# Revit family: DIGIDIM Mini Input Unit _444
name_source: partatom
category: Electrical Fixtures
revit_build: Autodesk Revit 2018 (Build: 20170223_1515(x64)
units: mm (PartAtom-declared; Revit-internal decimal feet)

## family parameters
Always vertical = No
Cut with Voids When Loaded = No
Maintain Annotation Orientation = No
OmniClass Number = 23.80.00.00
OmniClass Title = Electric Power and Lighting
Part Type = Normal
Room Calculation Point = No
Round Connector Dimension = Use Diameter
Shared = No
Work Plane-Based = Yes

## types (1)
- Mini Input UNIT
    Ambient temperature = 0 °C to +40 °C
    Cable length = 170mm. Do NOT increase length of switch input cable.
    DALI Connection = Ribbon cable terminated with
1.2 mm ferrules.
    DALI consumption = 10 mA
    DALI supply output = None (Use external DALI power supply.)
    Debounce period = 50 ms
    Default Elevation = 0 mm  [stored 0 ft]
    Dimensions: = Encapsulated printed circuit board
    EMC emission = EN 55015
    EMC immunity = EN 61547
    Environment = Complies with WEEE and RoHS
directives
    IP code: = IP20
    Inputs: = 4 inputs (active low)
COM Input Ground
    Isolation = No isolation from DALI network: switches must provide user protection.
    Manufacturer = 444
    Mounting = For installation in a suitably enclosed location only.
    Overload protection = ± 7 V
    Relative humidity = Max. 90 %, noncondensing
    Safety = EN 61347-2-11
    Short-circuit current = 0.5 mA maximum
    Storage temperature = −10 °C to +70 °C
    Type Comments = Helvar
    Voltage-free switched inputs: = 5 V nominal with switch open,
must be less than 0.3 V with switch closed.
    Weight = 10 g

note: [stored X ft] marks values corroborated as IEEE doubles in the binary element streams (Revit-internal decimal feet)

## geometry (parser evidence)
native form markers: Sweep x3
no freeform markers — native parametric forms only
